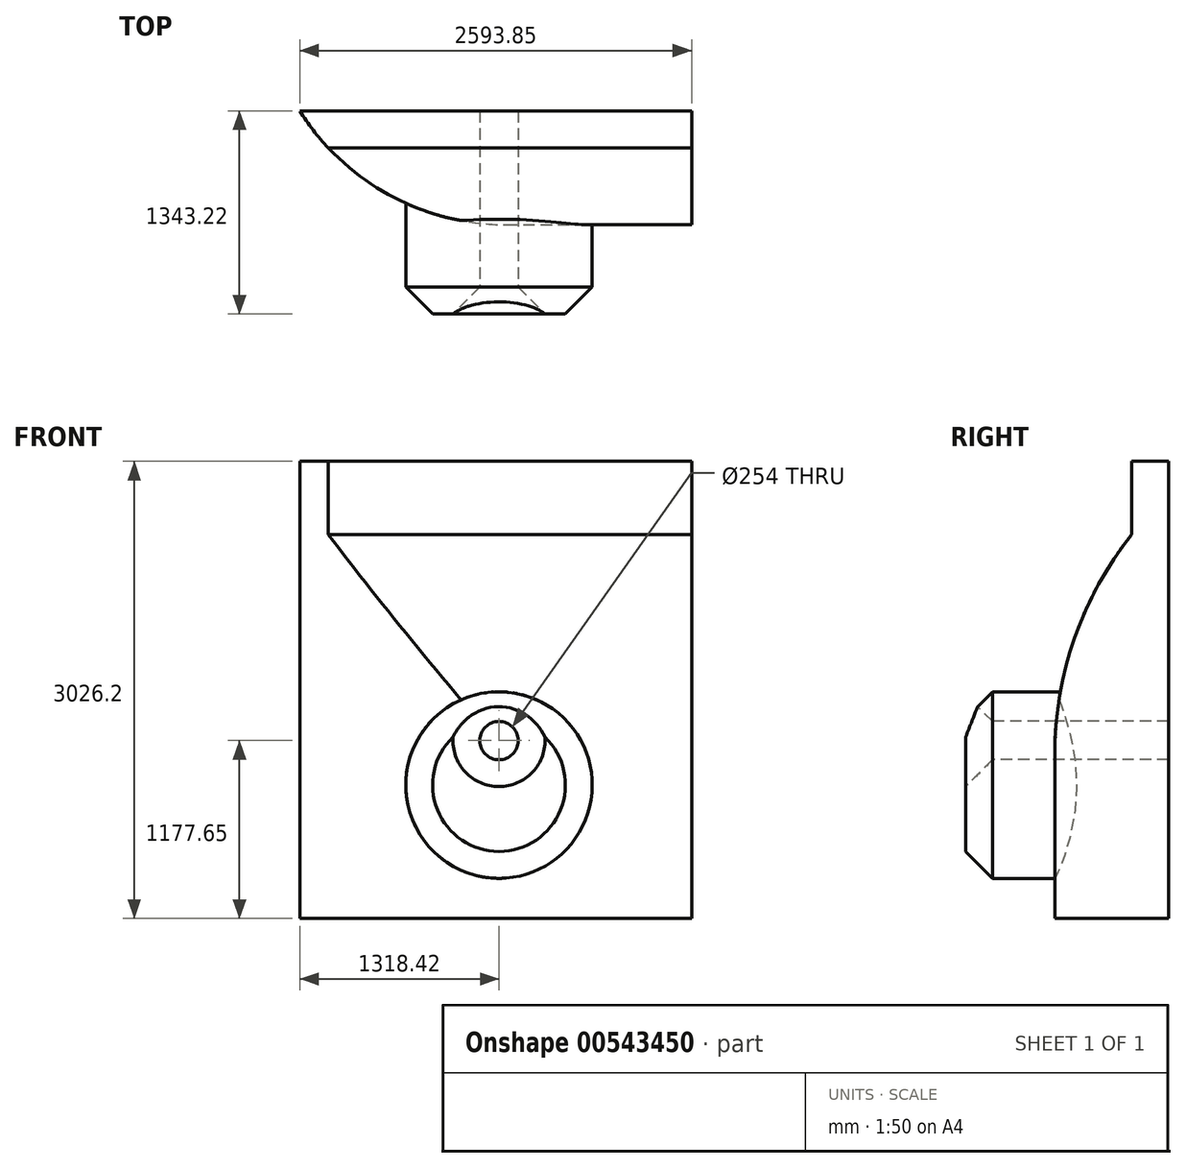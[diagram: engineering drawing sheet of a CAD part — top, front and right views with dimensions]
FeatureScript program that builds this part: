
annotation { "Feature Type Name" : "Feature", "Feature Type Description" : "" }
export const myFeature = defineFeature(function(context is Context, id is Id, definition is map)
    precondition{}
    {
        {
            var Q0;
            Q0=qCreatedBy(makeId("Front.planeOp"),FACE);
            var sketch = newSketch(context, id + "F0", { "sketchPlane" : qUnion([Q0])});
            skLineSegment(sketch, "E0.bottom", {"start": v(-1318.42, -1177.65) * mm, "end": v(1275.43, -1177.65) * mm});
            skLineSegment(sketch, "E0.top", {"start": v(-1318.42, 1362.35) * mm, "end": v(1275.43, 1362.35) * mm});
            skLineSegment(sketch, "E0.left", {"start": v(-1318.42, -1177.65) * mm, "end": v(-1318.42, 1362.35) * mm});
            skLineSegment(sketch, "E0.right", {"start": v(1275.43, -1177.65) * mm, "end": v(1275.43, 1362.35) * mm});
            skSolve(sketch);
        }
        {
            var Q0;
            Q0=makeQuery(id+"F0.imprint","IMPRINT",FACE,{"disambiguationData":[TD([[makeQuery(id+"F0.imprint","IMPRINT",EDGE,{"derivedFrom":sQuery(id+"F0.wireOp",EDGE,"E0.bottom")}),1.0]])]});
            extrude(context, id + "F1", {"entities" : qUnion([Q0]), "depth" : 752.74 * mm, "offsetDistance" : 25.4 * mm});
        }
        {
            var Q0;
            Q0=makeQuery(id+"F1.opExtrude","CAP_EDGE",EDGE,{"disambiguationData":[OSD([sQuery(id+"F0.wireOp",EDGE,"E0.top")])],"isStart":false});
            chamfer(context, id + "F2", {"entities" : qUnion([Q0]), "width" : 508 * mm, "tangentPropagation" : true});
        }
        {
            var Q0;
            Q0=makeQuery(id+"F1.opExtrude","CAP_FACE",FACE,{"disambiguationData":[OSD([sQuery(id+"F0.wireOp",EDGE,"E0.bottom"),sQuery(id+"F0.wireOp",EDGE,"E0.top"),sQuery(id+"F0.wireOp",EDGE,"E0.left"),sQuery(id+"F0.wireOp",EDGE,"E0.right")])],"isStart":false});
            var sketch = newSketch(context, id + "F3", { "sketchPlane" : qUnion([Q0])});
            skCircle(sketch, "E1", {"center": v(0, -294.4) * mm, "radius": 617.24 * mm});
            skSolve(sketch);
        }
        {
            var Q0;
            Q0=makeQuery(id+"F3.imprint","IMPRINT",FACE,{"disambiguationData":[TD([[makeQuery(id+"F3.imprint","IMPRINT",EDGE,{"derivedFrom":sQuery(id+"F3.wireOp",EDGE,"E1")}),1.0]])]});
            extrude(context, id + "F4", {"entities" : qUnion([Q0]), "operationType" : NewBodyOperationType.ADD, "depth" : 590.47 * mm, "offsetDistance" : 25.4 * mm});
        }
        {
            var Q0;
            Q0=makeQuery(id+"F4.opExtrude","CAP_FACE",FACE,{"disambiguationData":[OSD([sQuery(id+"F3.wireOp",EDGE,"E1")])],"isStart":false});
            var sketch = newSketch(context, id + "F5", { "sketchPlane" : qUnion([Q0])});
            skSolve(sketch);
        }
        {
            var Q0;
            Q0=makeQuery(id+"F5.imprint","IMPRINT",FACE,{"disambiguationData":[TD([[makeQuery(id+"F5.imprint","IMPRINT",EDGE,{"derivedFrom":makeQuery(id+"F4.opExtrude","CAP_EDGE",EDGE,{"disambiguationData":[OSD([sQuery(id+"F3.wireOp",EDGE,"E1")])],"isStart":false})}),1.0]])]});
            var sketch = newSketch(context, id + "F6", { "sketchPlane" : qUnion([Q0])});
            skPoint(sketch, "E2", {"position": v(0, 0) * mm});
            skSolve(sketch);
        }
        {
            var Q0;
            Q0=sQuery(id+"F6.wireOp",VERTEX,"E2");
            var Q1;
            Q1=makeQuery(id+"F1.opExtrude","SWEPT_BODY",BODY,{"disambiguationData":[OSD([sQuery(id+"F0.wireOp",EDGE,"E0.bottom"),sQuery(id+"F0.wireOp",EDGE,"E0.top"),sQuery(id+"F0.wireOp",EDGE,"E0.left"),sQuery(id+"F0.wireOp",EDGE,"E0.right")])]});
            hole(context, id + "F7", {"style" : HoleStyle.SIMPLE, "endStyle" : HoleEndStyle.BLIND, "holeDiameter" : 254 * mm, "holeDepth" : 2540 * mm, "isTappedThrough" : true, "tappedDepth" : 12.7 * mm, "tapClearance" : 3, "locations" : qUnion([Q0]), "scope" : qUnion([Q1])});
        }
        {
            var Q0;
            Q0=makeQuery(id+"F1.opExtrude","SWEPT_FACE",FACE,{"disambiguationData":[OSD([sQuery(id+"F0.wireOp",EDGE,"E0.top")])]});
            extrude(context, id + "F8", {"entities" : qUnion([Q0]), "operationType" : NewBodyOperationType.ADD, "depth" : 486.2 * mm, "offsetDistance" : 25.4 * mm});
        }
        {
            var Q0;
            {var subQ0=sQuery(id+"F0.wireOp",EDGE,"E0.top");Q0=makeQuery(id+"F2.opChamfer","BLEND_EDGE",EDGE,{"blendedFrom":[makeQuery(id+"F1.opExtrude","CAP_EDGE",EDGE,{"disambiguationData":[OSD([subQ0])],"isStart":false}),makeQuery(id+"F1.opExtrude","CAP_FACE",FACE,{"disambiguationData":[OSD([sQuery(id+"F0.wireOp",EDGE,"E0.bottom"),subQ0,sQuery(id+"F0.wireOp",EDGE,"E0.left"),sQuery(id+"F0.wireOp",EDGE,"E0.right")])],"isStart":false})],"blendedInto":[makeQuery(id+"F1.opExtrude","CAP_FACE",FACE,{"disambiguationData":[OSD([sQuery(id+"F0.wireOp",EDGE,"E0.bottom"),subQ0,sQuery(id+"F0.wireOp",EDGE,"E0.left"),sQuery(id+"F0.wireOp",EDGE,"E0.right")])],"isStart":false})]});}
            fillet(context, id + "F9", {"entities" : qUnion([Q0]), "radius" : 2329.42 * mm, "tangentPropagation" : true, "allowEdgeOverflow" : false});
        }
        {
            var Q0;
            Q0=makeQuery(id+"F1.opExtrude","CAP_EDGE",EDGE,{"disambiguationData":[OSD([sQuery(id+"F0.wireOp",EDGE,"E0.left")])],"isStart":false});
            var Q1;
            {var subQ0=sQuery(id+"F0.wireOp",EDGE,"E0.left");var subQ1=sQuery(id+"F0.wireOp",EDGE,"E0.top");Q1=makeQuery(id+"F9.opFillet","BLEND_EDGE",EDGE,{"blendedFrom":[makeQuery(id+"F2.opChamfer","BLEND_EDGE",EDGE,{"blendedFrom":[makeQuery(id+"F1.opExtrude","CAP_EDGE",EDGE,{"disambiguationData":[OSD([subQ1])],"isStart":false}),makeQuery(id+"F1.opExtrude","CAP_FACE",FACE,{"disambiguationData":[OSD([sQuery(id+"F0.wireOp",EDGE,"E0.bottom"),subQ1,subQ0,sQuery(id+"F0.wireOp",EDGE,"E0.right")])],"isStart":false})],"blendedInto":[makeQuery(id+"F1.opExtrude","CAP_FACE",FACE,{"disambiguationData":[OSD([sQuery(id+"F0.wireOp",EDGE,"E0.bottom"),subQ1,subQ0,sQuery(id+"F0.wireOp",EDGE,"E0.right")])],"isStart":false})]}),makeQuery(id+"F8.boolean.opBoolean","MERGE",FACE,{"derivedFrom":[makeQuery(id+"F1.opExtrude","SWEPT_FACE",FACE,{"disambiguationData":[OSD([subQ0])]}),makeQuery(id+"F8.opExtrude","SWEPT_FACE",FACE,{"disambiguationData":[OSD([subQ1,subQ0])]})]})],"blendedInto":[makeQuery(id+"F8.boolean.opBoolean","MERGE",FACE,{"derivedFrom":[makeQuery(id+"F1.opExtrude","SWEPT_FACE",FACE,{"disambiguationData":[OSD([subQ0])]}),makeQuery(id+"F8.opExtrude","SWEPT_FACE",FACE,{"disambiguationData":[OSD([subQ1,subQ0])]})]})]});}
            fillet(context, id + "F10", {"entities" : qUnion([Q0, Q1]), "radius" : 1613.3 * mm, "tangentPropagation" : true, "allowEdgeOverflow" : false});
        }
        {
            var Q0;
            Q0=makeQuery(id+"F4.opExtrude","CAP_FACE",FACE,{"disambiguationData":[OSD([sQuery(id+"F3.wireOp",EDGE,"E1")])],"isStart":false});
            chamfer(context, id + "F11", {"entities" : qUnion([Q0]), "width" : 177.8 * mm, "tangentPropagation" : true});
        }
    });
